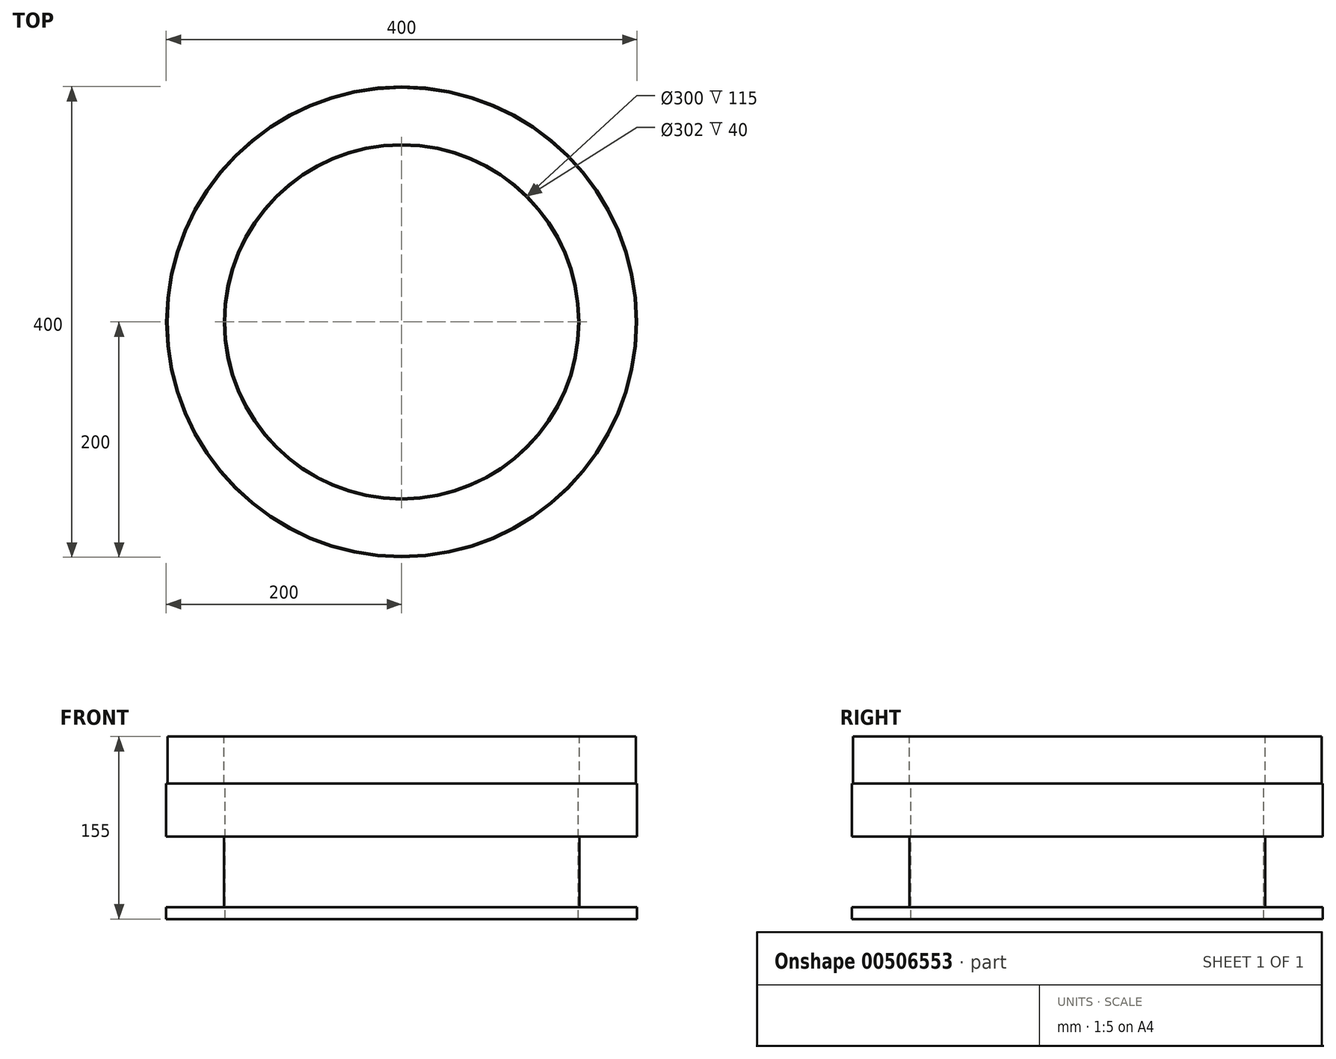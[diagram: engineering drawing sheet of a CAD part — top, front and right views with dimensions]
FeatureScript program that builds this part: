
annotation { "Feature Type Name" : "Feature", "Feature Type Description" : "" }
export const myFeature = defineFeature(function(context is Context, id is Id, definition is map)
    precondition{}
    {
        {
            var Q0;
            Q0=qCreatedBy(makeId("Front.planeOp"),FACE);
            var sketch = newSketch(context, id + "F0", { "sketchPlane" : qUnion([Q0])});
            skLineSegment(sketch, "E0", {"start": v(0, 710.75) * mm, "end": v(0, -704.58) * mm, "construction": true});
            skLineSegment(sketch, "E1", {"start": v(-150, 300.65) * mm, "end": v(-150, 415.65) * mm});
            skLineSegment(sketch, "E2", {"start": v(-150, 415.65) * mm, "end": v(-151, 415.65) * mm});
            skLineSegment(sketch, "E3", {"start": v(-199, 415.65) * mm, "end": v(-200, 415.65) * mm});
            skLineSegment(sketch, "E4", {"start": v(-200, 415.65) * mm, "end": v(-200, 370.65) * mm});
            skLineSegment(sketch, "E5", {"start": v(-200, 370.65) * mm, "end": v(-151, 370.65) * mm});
            skLineSegment(sketch, "E6", {"start": v(-151, 370.65) * mm, "end": v(-151, 310.65) * mm});
            skLineSegment(sketch, "E7", {"start": v(-151, 310.65) * mm, "end": v(-200, 310.65) * mm});
            skLineSegment(sketch, "E8", {"start": v(-200, 310.65) * mm, "end": v(-200, 300.65) * mm});
            skLineSegment(sketch, "E9", {"start": v(-200, 300.65) * mm, "end": v(-150, 300.65) * mm});
            skLineSegment(sketch, "E10", {"start": v(-199, 455.65) * mm, "end": v(-199, 415.65) * mm});
            skLineSegment(sketch, "E11", {"start": v(-199, 455.65) * mm, "end": v(-151, 455.65) * mm});
            skLineSegment(sketch, "E12", {"start": v(-151, 415.65) * mm, "end": v(-151, 455.65) * mm});
            skSolve(sketch);
        }
        {
            var Q0;
            Q0=qSketchRegion(id+"F0",true);
            var Q1;
            Q1=sQuery(id+"F0.wireOp",EDGE,"E0");
            revolve(context, id + "F1", {"entities" : qUnion([Q0]), "axis" : qUnion([Q1]), "revolveType" : RevolveType.FULL});
        }
    });
